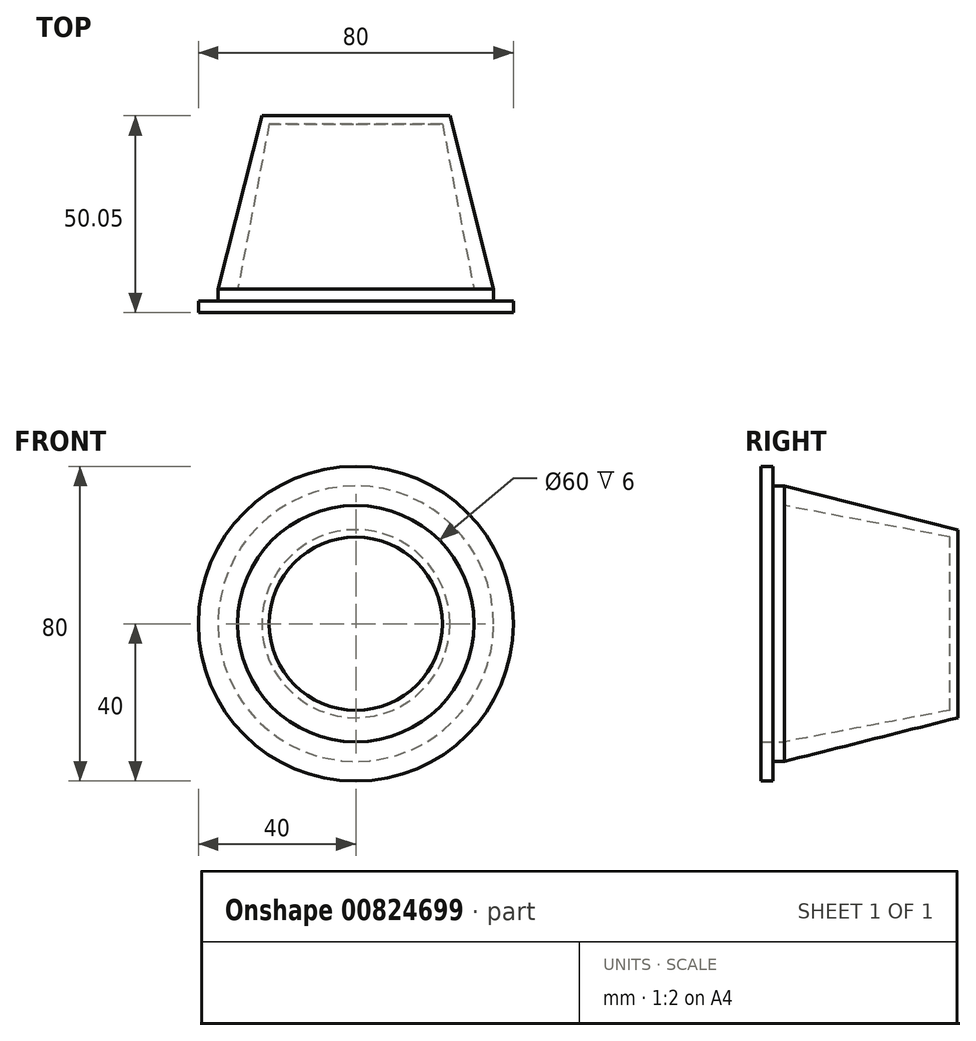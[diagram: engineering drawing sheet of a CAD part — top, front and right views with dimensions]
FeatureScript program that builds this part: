
annotation { "Feature Type Name" : "Feature", "Feature Type Description" : "" }
export const myFeature = defineFeature(function(context is Context, id is Id, definition is map)
    precondition{}
    {
        {
            var Q0;
            Q0=qCreatedBy(makeId("Front.planeOp"),FACE);
            var sketch = newSketch(context, id + "F0", { "sketchPlane" : qUnion([Q0])});
            skCircle(sketch, "E0", {"center": v(0, 0) * mm, "radius": 40 * mm});
            skCircle(sketch, "E1", {"center": v(0, 0) * mm, "radius": 30 * mm});
            skSolve(sketch);
        }
        {
            var Q0;
            Q0=qSketchRegion(id+"F0",true);
            extrude(context, id + "F1", {"entities" : qUnion([Q0]), "depth" : 3 * mm, "offsetDistance" : 25 * mm});
        }
        {
            var Q0;
            Q0=qCreatedBy(makeId("Front.planeOp"),FACE);
            var sketch = newSketch(context, id + "F2", { "sketchPlane" : qUnion([Q0])});
            skCircle(sketch, "E2", {"center": v(0, 0) * mm, "radius": 30 * mm});
            skCircle(sketch, "E3", {"center": v(0, 0) * mm, "radius": 35 * mm});
            skSolve(sketch);
        }
        {
            var Q0;
            Q0=qSketchRegion(id+"F2",true);
            extrude(context, id + "F3", {"entities" : qUnion([Q0]), "operationType" : NewBodyOperationType.ADD, "oppositeDirection" : true, "depth" : 3 * mm, "offsetDistance" : 25 * mm});
        }
        {
            var Q0;
            Q0=qCreatedBy(makeId("Front.planeOp"),FACE);
            cPlane(context, id + "F4", {"entities" : qUnion([Q0]), "cplaneType" : CPlaneType.OFFSET, "offset" : 47.05 * mm, "oppositeDirection" : true, "width" : 150 * mm, "height" : 150 * mm});
        }
        {
            var Q0;
            Q0=qCreatedBy(id+"F4.planeOp",FACE);
            var sketch = newSketch(context, id + "F5", { "sketchPlane" : qUnion([Q0])});
            skCircle(sketch, "E4", {"center": v(0, 0) * mm, "radius": 23.87 * mm});
            skSolve(sketch);
        }
        {
            var Q0;
            Q0=makeQuery(id+"F3.opExtrude","CAP_FACE",FACE,{"disambiguationData":[OSD([sQuery(id+"F2.wireOp",EDGE,"E2"),sQuery(id+"F2.wireOp",EDGE,"E3")])],"isStart":false});
            var sketch = newSketch(context, id + "F6", { "sketchPlane" : qUnion([Q0])});
            skCircle(sketch, "E5", {"center": v(0, 0) * mm, "radius": 35 * mm});
            skSolve(sketch);
        }
        {
            var Q1;
            Q1=qSketchRegion(id+"F5",true);
            var Q2;
            Q2=qSketchRegion(id+"F6",true);
            loft(context, id + "F7", {"operationType" : NewBodyOperationType.ADD, "sheetProfilesArray" : [{ "sheetProfileEntities" : qUnion([Q1]) }, { "sheetProfileEntities" : qUnion([Q2]) }]});
        }
        {
            var Q0;
            Q0=qCreatedBy(makeId("Front.planeOp"),FACE);
            cPlane(context, id + "F8", {"entities" : qUnion([Q0]), "cplaneType" : CPlaneType.OFFSET, "offset" : 45 * mm, "oppositeDirection" : true, "width" : 150 * mm, "height" : 150 * mm});
        }
        {
            var Q0;
            Q0=qCreatedBy(id+"F8.planeOp",FACE);
            var sketch = newSketch(context, id + "F9", { "sketchPlane" : qUnion([Q0])});
            skCircle(sketch, "E6", {"center": v(0, 0) * mm, "radius": 22 * mm});
            skSolve(sketch);
        }
        {
            var Q0;
            Q0=makeQuery(id+"F7.opLoft","CAP_FACE",FACE,{"disambiguationData":[OSD([makeQuery(id+"F6.imprint","IMPRINT",FACE,{"disambiguationData":[TD([[makeQuery(id+"F6.imprint","IMPRINT",EDGE,{"derivedFrom":makeQuery(id+"F3.opExtrude","CAP_EDGE",EDGE,{"disambiguationData":[OSD([sQuery(id+"F2.wireOp",EDGE,"E2")])],"isStart":false})}),-1.0]])]})])],"isStart":true});
            var sketch = newSketch(context, id + "F10", { "sketchPlane" : qUnion([Q0])});
            skCircle(sketch, "E7", {"center": v(0, 0) * mm, "radius": 30 * mm});
            skSolve(sketch);
        }
        {
            var Q1;
            Q1=qSketchRegion(id+"F9",true);
            var Q2;
            Q2=qSketchRegion(id+"F10",true);
            loft(context, id + "F11", {"operationType" : NewBodyOperationType.REMOVE, "sheetProfilesArray" : [{ "sheetProfileEntities" : qUnion([Q1]) }, { "sheetProfileEntities" : qUnion([Q2]) }]});
        }
    });
